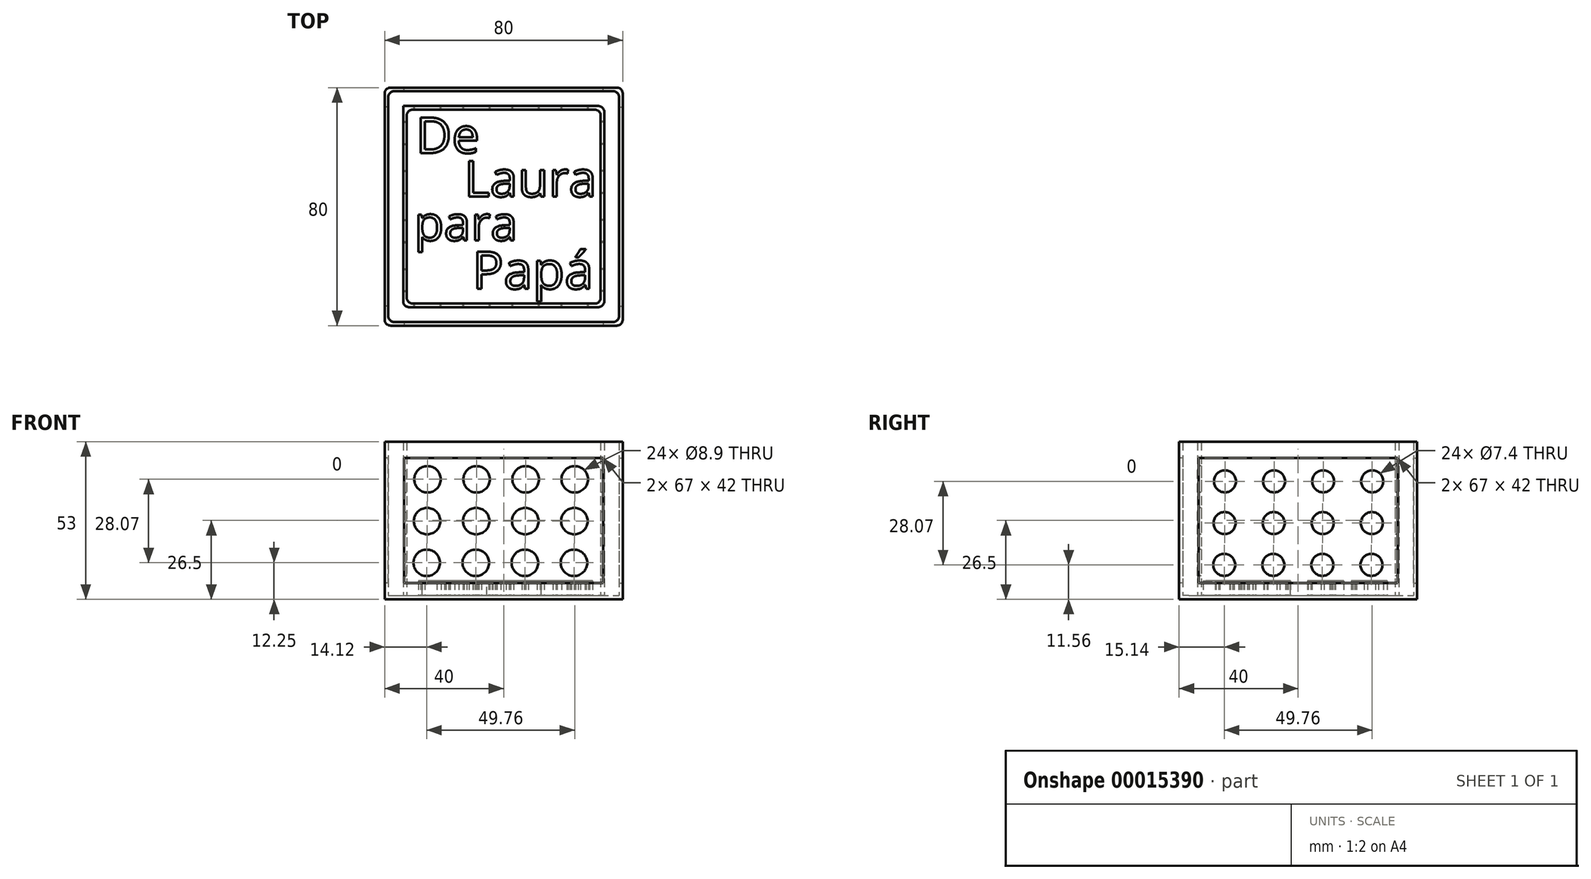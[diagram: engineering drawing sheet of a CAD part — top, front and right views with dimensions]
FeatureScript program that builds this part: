
annotation { "Feature Type Name" : "Feature", "Feature Type Description" : "" }
export const myFeature = defineFeature(function(context is Context, id is Id, definition is map)
    precondition{}
    {
        {
            var Q0;
            Q0=qCreatedBy(makeId("Front.planeOp"),FACE);
            var sketch = newSketch(context, id + "F0", { "sketchPlane" : qUnion([Q0])});
            skLineSegment(sketch, "E0.bottom", {"start": v(-40, 0) * mm, "end": v(40, 0) * mm});
            skLineSegment(sketch, "E0.top", {"start": v(-40, -53) * mm, "end": v(40, -53) * mm});
            skLineSegment(sketch, "E0.left", {"start": v(-40, 0) * mm, "end": v(-40, -53) * mm});
            skLineSegment(sketch, "E0.right", {"start": v(40, 0) * mm, "end": v(40, -53) * mm});
            skLineSegment(sketch, "E1", {"start": v(0, 20.93) * mm, "end": v(0, -63.26) * mm, "construction": true});
            skSolve(sketch);
        }
        {
            var Q0;
            Q0 = qSketchRegion(id + "F0", true);
            extrude(context, id + "F1", {"entities" : qUnion([Q0]), "depth" : 80 * mm});
        }
        {
            var Q0;
            Q0=makeQuery(id+"F1.opExtrude","SWEPT_FACE",FACE,{"disambiguationData":[OSD([sQuery(id+"F0.wireOp",EDGE,"E0.bottom")])]});
            shell(context, id + "F2", {"entities" : qUnion([Q0]), "thickness" : 1.2 * mm});
        }
        {
            var Q0;
            Q0=makeQuery(id+"F1.opExtrude","CAP_FACE",FACE,{"disambiguationData":[OSD([sQuery(id+"F0.wireOp",EDGE,"E0.bottom"),sQuery(id+"F0.wireOp",EDGE,"E0.top"),sQuery(id+"F0.wireOp",EDGE,"E0.left"),sQuery(id+"F0.wireOp",EDGE,"E0.right")])],"isStart":false});
            var sketch = newSketch(context, id + "F3", { "sketchPlane" : qUnion([Q0])});
            skLineSegment(sketch, "E2.0", {"start": v(-33.5, -5.5) * mm, "end": v(33.5, -5.5) * mm});
            skLineSegment(sketch, "E2.1", {"start": v(-33.5, -5.5) * mm, "end": v(-33.5, -47.5) * mm});
            skLineSegment(sketch, "E2.2", {"start": v(-33.5, -47.5) * mm, "end": v(33.5, -47.5) * mm});
            skLineSegment(sketch, "E2.3", {"start": v(33.5, -5.5) * mm, "end": v(33.5, -47.5) * mm});
            skSolve(sketch);
        }
        {
            var Q0;
            Q0 = qSketchRegion(id + "F3", true);
            extrude(context, id + "F4", {"entities" : qUnion([Q0]), "operationType" : NewBodyOperationType.REMOVE, "oppositeDirection" : true, "depth" : 3 * mm});
        }
        {
            var Q0;
            Q0=makeQuery(id+"F2.opShell","OFFSET_FACE",FACE,{"disambiguationData":[OSD([sQuery(id+"F0.wireOp",EDGE,"E0.top")])]});
            var sketch = newSketch(context, id + "F5", { "sketchPlane" : qUnion([Q0])});
            skLineSegment(sketch, "E3.0", {"start": v(33.8, -73.8) * mm, "end": v(33.8, -6.2) * mm});
            skLineSegment(sketch, "E3.1", {"start": v(-33.8, -73.8) * mm, "end": v(33.8, -73.8) * mm});
            skLineSegment(sketch, "E3.2", {"start": v(-33.8, -73.8) * mm, "end": v(-33.8, -6.2) * mm});
            skLineSegment(sketch, "E3.3", {"start": v(-33.8, -6.2) * mm, "end": v(33.8, -6.2) * mm});
            skLineSegment(sketch, "E4.0", {"start": v(32.6, -72.6) * mm, "end": v(32.6, -7.4) * mm});
            skLineSegment(sketch, "E4.1", {"start": v(-32.6, -72.6) * mm, "end": v(32.6, -72.6) * mm});
            skLineSegment(sketch, "E4.2", {"start": v(-32.6, -72.6) * mm, "end": v(-32.6, -7.4) * mm});
            skLineSegment(sketch, "E4.3", {"start": v(-32.6, -7.4) * mm, "end": v(32.6, -7.4) * mm});
            skLineSegment(sketch, "E5.0", {"start": v(33.8, -6.2) * mm, "end": v(-33.8, -6.2) * mm});
            skLineSegment(sketch, "E5.3", {"start": v(-33.8, -6.2) * mm, "end": v(-33.8, -73.8) * mm});
            skSolve(sketch);
        }
        {
            var Q0;
            Q0=makeQuery(id+"F5.imprint","IMPRINT",FACE,{"disambiguationData":[TD([[makeQuery(id+"F5.imprint","IMPRINT",EDGE,{"derivedFrom":sQuery(id+"F5.wireOp",EDGE,"E4.0")}),-1.0]])]});
            var Q1;
            Q1=makeQuery(id+"F1.opExtrude","SWEPT_FACE",FACE,{"disambiguationData":[OSD([sQuery(id+"F0.wireOp",EDGE,"E0.bottom")])]});
            extrude(context, id + "F6", {"entities" : qUnion([Q0]), "operationType" : NewBodyOperationType.ADD, "endBound" : BoundingType.UP_TO_SURFACE, "endBoundEntityFace" : qUnion([Q1]), "depth" : 25 * mm});
        }
        {
            var Q0;
            Q0=makeQuery(id+"F6.boolean.opBoolean","SPLIT",FACE,{"disambiguationData":[TD([makeQuery(id+"F6.opExtrude","SWEPT_FACE",FACE,{"disambiguationData":[OSD([sQuery(id+"F5.wireOp",EDGE,"E4.0")])]})])],"derivedFrom":makeQuery(id+"F2.opShell","OFFSET_FACE",FACE,{"disambiguationData":[OSD([sQuery(id+"F0.wireOp",EDGE,"E0.top")])]})});
            var sketch = newSketch(context, id + "F7", { "sketchPlane" : qUnion([Q0])});
            skText(sketch, "E6", { "text": "De", "fontName": "OpenSans-Regular.ttf"});
            skText(sketch, "E7", { "text": "Laura", "fontName": "OpenSans-Regular.ttf"});
            skText(sketch, "E8", { "text": "para\n", "fontName": "OpenSans-Regular.ttf"});
            skText(sketch, "E9", { "text": "Papá", "fontName": "OpenSans-Regular.ttf"});
            const initialGuessF7  = {"E6": [-0.02957, -0.022, 1, 0, 0.01198], "E7": [-0.01333, -0.03667, 1, 0, 0.0121], "E8": [-0.03008, -0.0514, 1, 0, 0.01172], "E9": [-0.01063, -0.06766, 1, 0, 0.01263]};
            skSetInitialGuess(sketch, initialGuessF7);
            skSolve(sketch);
        }
        {
            var Q0;
            Q0 = qSketchRegion(id + "F7", true);
            extrude(context, id + "F8", {"entities" : qUnion([Q0]), "operationType" : NewBodyOperationType.ADD, "depth" : 5 * mm});
        }
        {
            var Q0;
            Q0=makeQuery(id+"F1.opExtrude","SWEPT_FACE",FACE,{"disambiguationData":[OSD([sQuery(id+"F0.wireOp",EDGE,"E0.left")])]});
            var sketch = newSketch(context, id + "F9", { "sketchPlane" : qUnion([Q0])});
            skLineSegment(sketch, "E10.0", {"start": v(6.5, -5.5) * mm, "end": v(73.5, -5.5) * mm});
            skLineSegment(sketch, "E10.1", {"start": v(6.5, -5.5) * mm, "end": v(6.5, -47.5) * mm});
            skLineSegment(sketch, "E10.2", {"start": v(6.5, -47.5) * mm, "end": v(73.5, -47.5) * mm});
            skLineSegment(sketch, "E10.3", {"start": v(73.5, -5.5) * mm, "end": v(73.5, -47.5) * mm});
            skSolve(sketch);
        }
        {
            var Q0;
            Q0 = qSketchRegion(id + "F9", true);
            extrude(context, id + "F10", {"entities" : qUnion([Q0]), "operationType" : NewBodyOperationType.REMOVE, "oppositeDirection" : true, "depth" : 2 * mm});
        }
        {
            var Q0;
            Q0=makeQuery(id+"F1.opExtrude","SWEPT_FACE",FACE,{"disambiguationData":[OSD([sQuery(id+"F0.wireOp",EDGE,"E0.right")])]});
            var sketch = newSketch(context, id + "F11", { "sketchPlane" : qUnion([Q0])});
            skLineSegment(sketch, "E11.0", {"start": v(-73.5, -5.5) * mm, "end": v(-6.5, -5.5) * mm});
            skLineSegment(sketch, "E11.1", {"start": v(-73.5, -5.5) * mm, "end": v(-73.5, -47.5) * mm});
            skLineSegment(sketch, "E11.2", {"start": v(-73.5, -47.5) * mm, "end": v(-6.5, -47.5) * mm});
            skLineSegment(sketch, "E11.3", {"start": v(-6.5, -5.5) * mm, "end": v(-6.5, -47.5) * mm});
            skSolve(sketch);
        }
        {
            var Q0;
            Q0=makeQuery(id+"F11.imprint","IMPRINT",FACE,{"disambiguationData":[TD([[makeQuery(id+"F11.imprint","IMPRINT",EDGE,{"derivedFrom":sQuery(id+"F11.wireOp",EDGE,"E11.0")}),-1.0]])]});
            var Q1;
            Q1=sQuery(id+"F11.wireOp",EDGE,"E11.0");
            var Q2;
            Q2=sQuery(id+"F11.wireOp",EDGE,"E11.1");
            var Q3;
            Q3=sQuery(id+"F11.wireOp",EDGE,"E11.2");
            var Q4;
            Q4=sQuery(id+"F11.wireOp",EDGE,"E11.3");
            extrude(context, id + "F12", {"entities" : qUnion([Q0]), "operationType" : NewBodyOperationType.REMOVE, "surfaceEntities" : qUnion([Q1, Q2, Q3, Q4]), "oppositeDirection" : true, "depth" : 2 * mm});
        }
        {
            var Q0;
            Q0=makeQuery(id+"F0.imprint","IMPRINT",FACE,{"disambiguationData":[TD([[makeQuery(id+"F0.imprint","IMPRINT",EDGE,{"derivedFrom":sQuery(id+"F0.wireOp",EDGE,"E0.bottom")}),-1.0]])]});
            var sketch = newSketch(context, id + "F13", { "sketchPlane" : qUnion([Q0])});
            skLineSegment(sketch, "E12.bottom", {"start": v(33.5, -5.5) * mm, "end": v(-33.5, -5.5) * mm});
            skLineSegment(sketch, "E12.top", {"start": v(33.5, -47.5) * mm, "end": v(-33.5, -47.5) * mm});
            skLineSegment(sketch, "E12.left", {"start": v(33.5, -5.5) * mm, "end": v(33.5, -47.5) * mm});
            skLineSegment(sketch, "E12.right", {"start": v(-33.5, -5.5) * mm, "end": v(-33.5, -47.5) * mm});
            skSolve(sketch);
        }
        {
            var Q0;
            Q0 = qSketchRegion(id + "F13", true);
            extrude(context, id + "F14", {"entities" : qUnion([Q0]), "operationType" : NewBodyOperationType.REMOVE, "depth" : 2 * mm});
        }
        {
            var Q0;
            Q0=makeQuery(id+"F6.opExtrude","SWEPT_FACE",FACE,{"disambiguationData":[OSD([sQuery(id+"F5.wireOp",EDGE,"E3.1")])]});
            var sketch = newSketch(context, id + "F15", { "sketchPlane" : qUnion([Q0])});
            skCircle(sketch, "E13", {"center": v(-25.62, -12.68) * mm, "radius": 4.45 * mm});
            skCircle(sketch, "E14.1.0.0", {"center": v(-9.12, -12.68) * mm, "radius": 4.45 * mm});
            skCircle(sketch, "E14.2.0.0", {"center": v(7.38, -12.68) * mm, "radius": 4.45 * mm});
            skCircle(sketch, "E14.3.0.0", {"center": v(23.88, -12.68) * mm, "radius": 4.45 * mm});
            skLineSegment(sketch, "E14.direction1", {"start": v(-25.62, -12.68) * mm, "end": v(-9.12, -12.68) * mm, "construction": true});
            skCircle(sketch, "E15.1.0.0", {"center": v(-25.75, -26.72) * mm, "radius": 4.45 * mm});
            skCircle(sketch, "E15.1.0.1", {"center": v(-9.25, -26.72) * mm, "radius": 4.45 * mm});
            skCircle(sketch, "E15.1.0.2", {"center": v(7.25, -26.72) * mm, "radius": 4.45 * mm});
            skCircle(sketch, "E15.1.0.3", {"center": v(23.75, -26.72) * mm, "radius": 4.45 * mm});
            skCircle(sketch, "E15.2.0.0", {"center": v(-25.88, -40.75) * mm, "radius": 4.45 * mm});
            skCircle(sketch, "E15.2.0.1", {"center": v(-9.38, -40.75) * mm, "radius": 4.45 * mm});
            skCircle(sketch, "E15.2.0.2", {"center": v(7.12, -40.75) * mm, "radius": 4.45 * mm});
            skCircle(sketch, "E15.2.0.3", {"center": v(23.62, -40.75) * mm, "radius": 4.45 * mm});
            skLineSegment(sketch, "E15.direction1", {"start": v(-25.62, -12.68) * mm, "end": v(-25.75, -26.72) * mm, "construction": true});
            skSolve(sketch);
        }
        {
            var Q0;
            Q0=makeQuery(id+"F15.imprint","IMPRINT",FACE,{"disambiguationData":[TD([[makeQuery(id+"F15.imprint","IMPRINT",EDGE,{"derivedFrom":sQuery(id+"F15.wireOp",EDGE,"E13")}),1.0]])]});
            var Q1;
            Q1=makeQuery(id+"F15.imprint","IMPRINT",FACE,{"disambiguationData":[TD([[makeQuery(id+"F15.imprint","IMPRINT",EDGE,{"derivedFrom":sQuery(id+"F15.wireOp",EDGE,"E14.1.0.0")}),1.0]])]});
            var Q2;
            Q2=makeQuery(id+"F15.imprint","IMPRINT",FACE,{"disambiguationData":[TD([[makeQuery(id+"F15.imprint","IMPRINT",EDGE,{"derivedFrom":sQuery(id+"F15.wireOp",EDGE,"E14.2.0.0")}),1.0]])]});
            var Q3;
            Q3=makeQuery(id+"F15.imprint","IMPRINT",FACE,{"disambiguationData":[TD([[makeQuery(id+"F15.imprint","IMPRINT",EDGE,{"derivedFrom":sQuery(id+"F15.wireOp",EDGE,"E14.3.0.0")}),1.0]])]});
            var Q4;
            Q4=makeQuery(id+"F15.imprint","IMPRINT",FACE,{"disambiguationData":[TD([[makeQuery(id+"F15.imprint","IMPRINT",EDGE,{"derivedFrom":sQuery(id+"F15.wireOp",EDGE,"E15.1.0.3")}),1.0]])]});
            var Q5;
            Q5=makeQuery(id+"F15.imprint","IMPRINT",FACE,{"disambiguationData":[TD([[makeQuery(id+"F15.imprint","IMPRINT",EDGE,{"derivedFrom":sQuery(id+"F15.wireOp",EDGE,"E15.1.0.2")}),1.0]])]});
            var Q6;
            Q6=makeQuery(id+"F15.imprint","IMPRINT",FACE,{"disambiguationData":[TD([[makeQuery(id+"F15.imprint","IMPRINT",EDGE,{"derivedFrom":sQuery(id+"F15.wireOp",EDGE,"E15.1.0.1")}),1.0]])]});
            var Q7;
            Q7=makeQuery(id+"F15.imprint","IMPRINT",FACE,{"disambiguationData":[TD([[makeQuery(id+"F15.imprint","IMPRINT",EDGE,{"derivedFrom":sQuery(id+"F15.wireOp",EDGE,"E15.1.0.0")}),1.0]])]});
            var Q8;
            Q8=makeQuery(id+"F15.imprint","IMPRINT",FACE,{"disambiguationData":[TD([[makeQuery(id+"F15.imprint","IMPRINT",EDGE,{"derivedFrom":sQuery(id+"F15.wireOp",EDGE,"E15.2.0.1")}),1.0]])]});
            var Q9;
            Q9=makeQuery(id+"F15.imprint","IMPRINT",FACE,{"disambiguationData":[TD([[makeQuery(id+"F15.imprint","IMPRINT",EDGE,{"derivedFrom":sQuery(id+"F15.wireOp",EDGE,"E15.2.0.2")}),1.0]])]});
            var Q10;
            Q10=makeQuery(id+"F15.imprint","IMPRINT",FACE,{"disambiguationData":[TD([[makeQuery(id+"F15.imprint","IMPRINT",EDGE,{"derivedFrom":sQuery(id+"F15.wireOp",EDGE,"E15.2.0.3")}),1.0]])]});
            var Q11;
            Q11=makeQuery(id+"F15.imprint","IMPRINT",FACE,{"disambiguationData":[TD([[makeQuery(id+"F15.imprint","IMPRINT",EDGE,{"derivedFrom":sQuery(id+"F15.wireOp",EDGE,"E15.2.0.0")}),1.0]])]});
            var Q12;
            Q12=sQuery(id+"F15.wireOp",EDGE,"E13");
            var Q13;
            Q13=sQuery(id+"F15.wireOp",EDGE,"E14.1.0.0");
            var Q14;
            Q14=sQuery(id+"F15.wireOp",EDGE,"E14.2.0.0");
            var Q15;
            Q15=sQuery(id+"F15.wireOp",EDGE,"E14.3.0.0");
            var Q16;
            Q16=sQuery(id+"F15.wireOp",EDGE,"E15.1.0.3");
            var Q17;
            Q17=sQuery(id+"F15.wireOp",EDGE,"E15.1.0.2");
            var Q18;
            Q18=sQuery(id+"F15.wireOp",EDGE,"E15.1.0.1");
            var Q19;
            Q19=sQuery(id+"F15.wireOp",EDGE,"E15.1.0.0");
            var Q20;
            Q20=sQuery(id+"F15.wireOp",EDGE,"E15.2.0.0");
            var Q21;
            Q21=sQuery(id+"F15.wireOp",EDGE,"E15.2.0.1");
            var Q22;
            Q22=sQuery(id+"F15.wireOp",EDGE,"E15.2.0.2");
            var Q23;
            Q23=sQuery(id+"F15.wireOp",EDGE,"E15.2.0.3");
            extrude(context, id + "F16", {"entities" : qUnion([Q0, Q1, Q2, Q3, Q4, Q5, Q6, Q7, Q8, Q9, Q10, Q11]), "operationType" : NewBodyOperationType.REMOVE, "surfaceEntities" : qUnion([Q12, Q13, Q14, Q15, Q16, Q17, Q18, Q19, Q20, Q21, Q22, Q23]), "endBound" : BoundingType.THROUGH_ALL, "oppositeDirection" : true, "depth" : 25 * mm});
        }
        {
            var Q0;
            Q0=makeQuery(id+"F6.opExtrude","SWEPT_FACE",FACE,{"disambiguationData":[OSD([sQuery(id+"F5.wireOp",EDGE,"E4.2")])]});
            var sketch = newSketch(context, id + "F17", { "sketchPlane" : qUnion([Q0])});
            skCircle(sketch, "E16", {"center": v(-64.6, -13.37) * mm, "radius": 3.7 * mm});
            skCircle(sketch, "E17.1.0.0", {"center": v(-48.1, -13.37) * mm, "radius": 3.7 * mm});
            skCircle(sketch, "E17.2.0.0", {"center": v(-31.6, -13.37) * mm, "radius": 3.7 * mm});
            skCircle(sketch, "E17.3.0.0", {"center": v(-15.1, -13.37) * mm, "radius": 3.7 * mm});
            skLineSegment(sketch, "E17.direction1", {"start": v(-64.6, -13.37) * mm, "end": v(-48.1, -13.37) * mm, "construction": true});
            skCircle(sketch, "E18.1.0.0", {"center": v(-64.73, -27.4) * mm, "radius": 3.7 * mm});
            skCircle(sketch, "E18.1.0.1", {"center": v(-48.23, -27.4) * mm, "radius": 3.7 * mm});
            skCircle(sketch, "E18.1.0.2", {"center": v(-31.73, -27.4) * mm, "radius": 3.7 * mm});
            skCircle(sketch, "E18.1.0.3", {"center": v(-15.23, -27.4) * mm, "radius": 3.7 * mm});
            skCircle(sketch, "E18.2.0.0", {"center": v(-64.86, -41.44) * mm, "radius": 3.7 * mm});
            skCircle(sketch, "E18.2.0.1", {"center": v(-48.36, -41.44) * mm, "radius": 3.7 * mm});
            skCircle(sketch, "E18.2.0.2", {"center": v(-31.86, -41.44) * mm, "radius": 3.7 * mm});
            skCircle(sketch, "E18.2.0.3", {"center": v(-15.36, -41.44) * mm, "radius": 3.7 * mm});
            skLineSegment(sketch, "E18.direction1", {"start": v(-64.6, -13.37) * mm, "end": v(-64.73, -27.4) * mm, "construction": true});
            skSolve(sketch);
        }
        {
            var Q0;
            Q0=makeQuery(id+"F17.imprint","IMPRINT",FACE,{"disambiguationData":[TD([[makeQuery(id+"F17.imprint","IMPRINT",EDGE,{"derivedFrom":sQuery(id+"F17.wireOp",EDGE,"E18.1.0.0")}),1.0]])]});
            var Q1;
            Q1=makeQuery(id+"F17.imprint","IMPRINT",FACE,{"disambiguationData":[TD([[makeQuery(id+"F17.imprint","IMPRINT",EDGE,{"derivedFrom":sQuery(id+"F17.wireOp",EDGE,"E18.2.0.0")}),1.0]])]});
            var Q2;
            Q2=makeQuery(id+"F17.imprint","IMPRINT",FACE,{"disambiguationData":[TD([[makeQuery(id+"F17.imprint","IMPRINT",EDGE,{"derivedFrom":sQuery(id+"F17.wireOp",EDGE,"E18.1.0.1")}),1.0]])]});
            var Q3;
            Q3=makeQuery(id+"F17.imprint","IMPRINT",FACE,{"disambiguationData":[TD([[makeQuery(id+"F17.imprint","IMPRINT",EDGE,{"derivedFrom":sQuery(id+"F17.wireOp",EDGE,"E17.1.0.0")}),1.0]])]});
            var Q4;
            Q4=makeQuery(id+"F17.imprint","IMPRINT",FACE,{"disambiguationData":[TD([[makeQuery(id+"F17.imprint","IMPRINT",EDGE,{"derivedFrom":sQuery(id+"F17.wireOp",EDGE,"E18.2.0.1")}),1.0]])]});
            var Q5;
            Q5=makeQuery(id+"F17.imprint","IMPRINT",FACE,{"disambiguationData":[TD([[makeQuery(id+"F17.imprint","IMPRINT",EDGE,{"derivedFrom":sQuery(id+"F17.wireOp",EDGE,"E18.2.0.2")}),1.0]])]});
            var Q6;
            Q6=makeQuery(id+"F17.imprint","IMPRINT",FACE,{"disambiguationData":[TD([[makeQuery(id+"F17.imprint","IMPRINT",EDGE,{"derivedFrom":sQuery(id+"F17.wireOp",EDGE,"E18.1.0.2")}),1.0]])]});
            var Q7;
            Q7=makeQuery(id+"F17.imprint","IMPRINT",FACE,{"disambiguationData":[TD([[makeQuery(id+"F17.imprint","IMPRINT",EDGE,{"derivedFrom":sQuery(id+"F17.wireOp",EDGE,"E17.2.0.0")}),1.0]])]});
            var Q8;
            Q8=makeQuery(id+"F17.imprint","IMPRINT",FACE,{"disambiguationData":[TD([[makeQuery(id+"F17.imprint","IMPRINT",EDGE,{"derivedFrom":sQuery(id+"F17.wireOp",EDGE,"E17.3.0.0")}),1.0]])]});
            var Q9;
            Q9=makeQuery(id+"F17.imprint","IMPRINT",FACE,{"disambiguationData":[TD([[makeQuery(id+"F17.imprint","IMPRINT",EDGE,{"derivedFrom":sQuery(id+"F17.wireOp",EDGE,"E18.2.0.3")}),1.0]])]});
            var Q10;
            Q10=makeQuery(id+"F17.imprint","IMPRINT",FACE,{"disambiguationData":[TD([[makeQuery(id+"F17.imprint","IMPRINT",EDGE,{"derivedFrom":sQuery(id+"F17.wireOp",EDGE,"E18.1.0.3")}),1.0]])]});
            var Q11;
            Q11=makeQuery(id+"F17.imprint","IMPRINT",FACE,{"disambiguationData":[TD([[makeQuery(id+"F17.imprint","IMPRINT",EDGE,{"derivedFrom":sQuery(id+"F17.wireOp",EDGE,"E16")}),1.0]])]});
            var Q12;
            Q12=sQuery(id+"F17.wireOp",EDGE,"E18.1.0.0");
            var Q13;
            Q13=sQuery(id+"F17.wireOp",EDGE,"E16");
            var Q14;
            Q14=sQuery(id+"F17.wireOp",EDGE,"E17.1.0.0");
            var Q15;
            Q15=sQuery(id+"F17.wireOp",EDGE,"E17.2.0.0");
            var Q16;
            Q16=sQuery(id+"F17.wireOp",EDGE,"E18.1.0.1");
            var Q17;
            Q17=sQuery(id+"F17.wireOp",EDGE,"E18.2.0.1");
            var Q18;
            Q18=sQuery(id+"F17.wireOp",EDGE,"E18.2.0.2");
            var Q19;
            Q19=sQuery(id+"F17.wireOp",EDGE,"E18.1.0.2");
            var Q20;
            Q20=sQuery(id+"F17.wireOp",EDGE,"E18.2.0.0");
            var Q21;
            Q21=sQuery(id+"F17.wireOp",EDGE,"E17.3.0.0");
            var Q22;
            Q22=sQuery(id+"F17.wireOp",EDGE,"E18.1.0.3");
            var Q23;
            Q23=sQuery(id+"F17.wireOp",EDGE,"E18.2.0.3");
            extrude(context, id + "F18", {"entities" : qUnion([Q0, Q1, Q2, Q3, Q4, Q5, Q6, Q7, Q8, Q9, Q10, Q11]), "operationType" : NewBodyOperationType.REMOVE, "surfaceEntities" : qUnion([Q12, Q13, Q14, Q15, Q16, Q17, Q18, Q19, Q20, Q21, Q22, Q23]), "endBound" : BoundingType.THROUGH_ALL, "depth" : 25 * mm});
        }
        {
            var Q0;
            Q0 = qSketchRegion(id + "F17", true);
            extrude(context, id + "F19", {"entities" : qUnion([Q0]), "operationType" : NewBodyOperationType.REMOVE, "oppositeDirection" : true, "depth" : 2 * mm});
        }
        {
            var Q0;
            Q0=makeQuery(id+"F1.opExtrude","CAP_EDGE",EDGE,{"disambiguationData":[OSD([sQuery(id+"F0.wireOp",EDGE,"E0.right")])],"isStart":false});
            var Q1;
            Q1=makeQuery(id+"F1.opExtrude","CAP_EDGE",EDGE,{"disambiguationData":[OSD([sQuery(id+"F0.wireOp",EDGE,"E0.left")])],"isStart":false});
            var Q2;
            Q2=makeQuery(id+"F1.opExtrude","CAP_EDGE",EDGE,{"disambiguationData":[OSD([sQuery(id+"F0.wireOp",EDGE,"E0.left")])],"isStart":true});
            var Q3;
            Q3=makeQuery(id+"F1.opExtrude","CAP_EDGE",EDGE,{"disambiguationData":[OSD([sQuery(id+"F0.wireOp",EDGE,"E0.right")])],"isStart":true});
            fillet(context, id + "F20", {"entities" : qUnion([Q0, Q1, Q2, Q3]), "radius" : 2 * mm, "tangentPropagation" : true, "allowEdgeOverflow" : false});
        }
        {
            var Q0;
            {var subQ0=sQuery(id+"F0.wireOp",EDGE,"E0.right");Q0=makeQuery(id+"F2.opShell","OFFSET_EDGE",EDGE,{"disambiguationData":[OSD([subQ0]),TDD([makeQuery(id+"F1.opExtrude","CAP_EDGE",EDGE,{"disambiguationData":[OSD([subQ0])],"isStart":true})])]});}
            var Q1;
            {var subQ0=sQuery(id+"F0.wireOp",EDGE,"E0.right");Q1=makeQuery(id+"F2.opShell","OFFSET_EDGE",EDGE,{"disambiguationData":[OSD([subQ0]),TDD([makeQuery(id+"F1.opExtrude","CAP_EDGE",EDGE,{"disambiguationData":[OSD([subQ0])],"isStart":false})])]});}
            var Q2;
            Q2=makeQuery(id+"F6.opExtrude","SWEPT_EDGE",EDGE,{"disambiguationData":[OSD([sQuery(id+"F5.wireOp",EDGE,"E4.0"),sQuery(id+"F5.wireOp",EDGE,"E4.1")])]});
            var Q3;
            Q3=makeQuery(id+"F6.opExtrude","SWEPT_EDGE",EDGE,{"disambiguationData":[OSD([sQuery(id+"F5.wireOp",EDGE,"E4.0"),sQuery(id+"F5.wireOp",EDGE,"E4.3")])]});
            var Q4;
            {var subQ0=sQuery(id+"F0.wireOp",EDGE,"E0.left");Q4=makeQuery(id+"F2.opShell","OFFSET_EDGE",EDGE,{"disambiguationData":[OSD([subQ0]),TDD([makeQuery(id+"F1.opExtrude","CAP_EDGE",EDGE,{"disambiguationData":[OSD([subQ0])],"isStart":true})])]});}
            var Q5;
            Q5=makeQuery(id+"F6.opExtrude","SWEPT_EDGE",EDGE,{"disambiguationData":[OSD([sQuery(id+"F5.wireOp",EDGE,"E4.2"),sQuery(id+"F5.wireOp",EDGE,"E4.3")])]});
            var Q6;
            Q6=makeQuery(id+"F6.opExtrude","SWEPT_EDGE",EDGE,{"disambiguationData":[OSD([sQuery(id+"F5.wireOp",EDGE,"E4.1"),sQuery(id+"F5.wireOp",EDGE,"E4.2")])]});
            var Q7;
            {var subQ0=sQuery(id+"F0.wireOp",EDGE,"E0.left");Q7=makeQuery(id+"F2.opShell","OFFSET_EDGE",EDGE,{"disambiguationData":[OSD([subQ0]),TDD([makeQuery(id+"F1.opExtrude","CAP_EDGE",EDGE,{"disambiguationData":[OSD([subQ0])],"isStart":false})])]});}
            var Q8;
            Q8=makeQuery(id+"F6.opExtrude","SWEPT_EDGE",EDGE,{"disambiguationData":[OSD([sQuery(id+"F5.wireOp",EDGE,"E3.0"),sQuery(id+"F5.wireOp",EDGE,"E3.1")])]});
            var Q9;
            Q9=makeQuery(id+"F6.opExtrude","SWEPT_EDGE",EDGE,{"disambiguationData":[OSD([sQuery(id+"F5.wireOp",EDGE,"E5.0"),sQuery(id+"F5.wireOp",EDGE,"E3.0")])]});
            var Q10;
            Q10=makeQuery(id+"F6.opExtrude","SWEPT_EDGE",EDGE,{"disambiguationData":[OSD([sQuery(id+"F5.wireOp",EDGE,"E5.0"),sQuery(id+"F5.wireOp",EDGE,"E5.3")])]});
            var Q11;
            Q11=makeQuery(id+"F6.opExtrude","SWEPT_EDGE",EDGE,{"disambiguationData":[OSD([sQuery(id+"F5.wireOp",EDGE,"E3.1"),sQuery(id+"F5.wireOp",EDGE,"E5.3")])]});
            fillet(context, id + "F21", {"entities" : qUnion([Q0, Q1, Q2, Q3, Q4, Q5, Q6, Q7, Q8, Q9, Q10, Q11]), "radius" : 2 * mm, "tangentPropagation" : true, "allowEdgeOverflow" : false});
        }
    });
